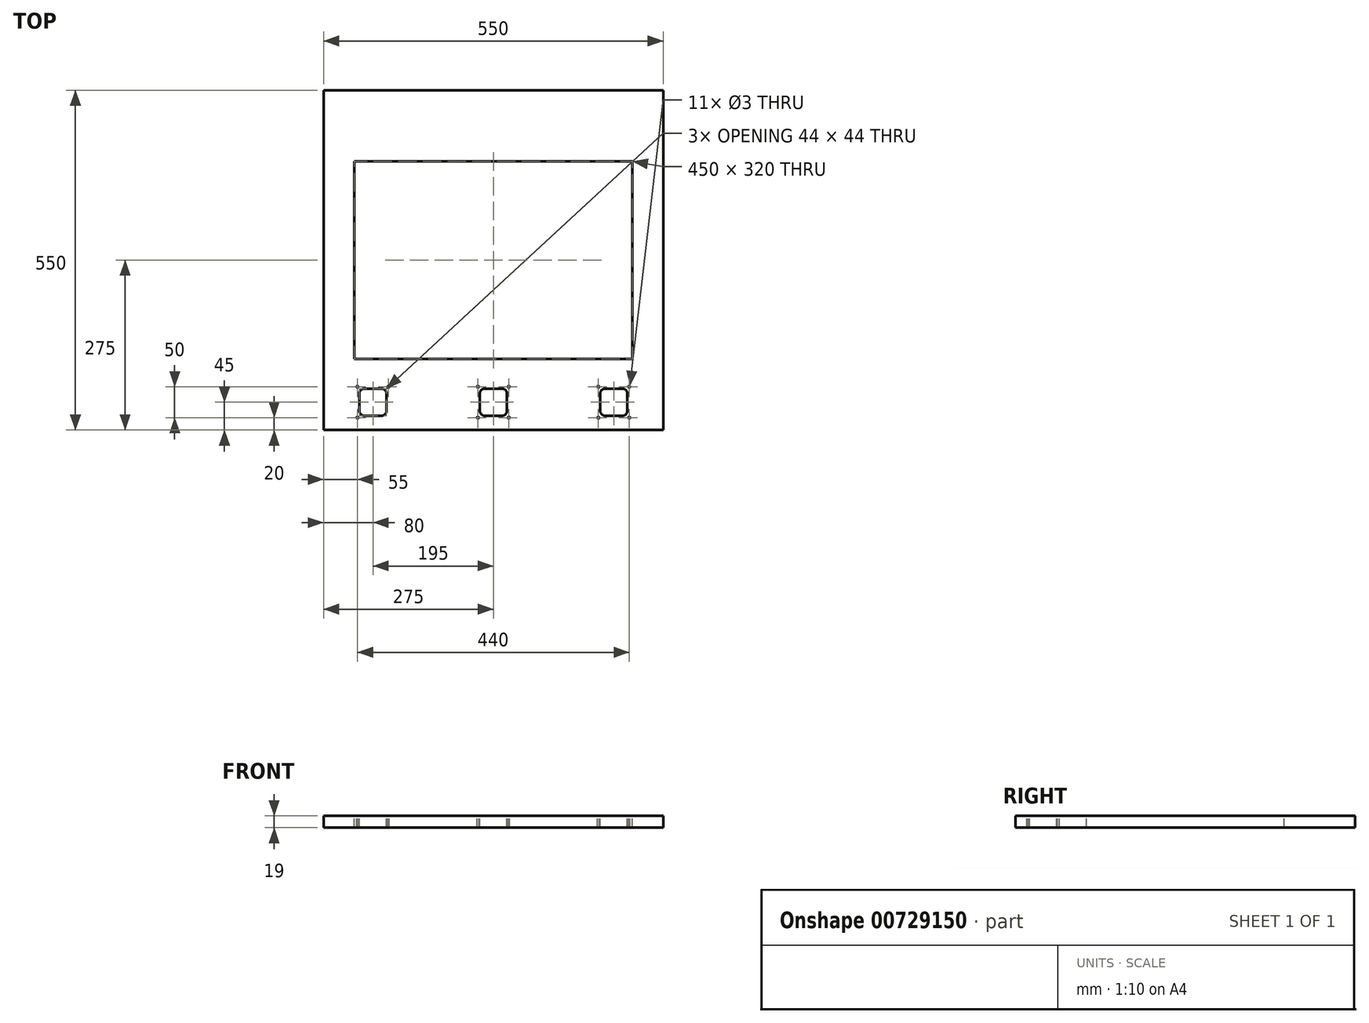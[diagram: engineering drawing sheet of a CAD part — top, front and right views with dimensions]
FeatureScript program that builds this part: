
annotation { "Feature Type Name" : "Feature", "Feature Type Description" : "" }
export const myFeature = defineFeature(function(context is Context, id is Id, definition is map)
    precondition{}
    {
        {
            var Q0;
            Q0=qCreatedBy(makeId("Top.planeOp"),FACE);
            var sketch = newSketch(context, id + "F0", { "sketchPlane" : qUnion([Q0])});
            skLineSegment(sketch, "E0.bottom", {"start": v(275, -275) * mm, "end": v(-275, -275) * mm});
            skLineSegment(sketch, "E0.top", {"start": v(275, 275) * mm, "end": v(-275, 275) * mm});
            skLineSegment(sketch, "E0.left", {"start": v(275, -275) * mm, "end": v(275, 275) * mm});
            skLineSegment(sketch, "E0.right", {"start": v(-275, -275) * mm, "end": v(-275, 275) * mm});
            skPoint(sketch, "E0.middle", {"position": v(0, 0) * mm});
            skSolve(sketch);
        }
        {
            var Q0;
            Q0=makeQuery(id+"F0.imprint","IMPRINT",FACE,{"disambiguationData":[TD([[makeQuery(id+"F0.imprint","IMPRINT",EDGE,{"derivedFrom":sQuery(id+"F0.wireOp",EDGE,"E0.bottom")}),-1.0]])]});
            extrude(context, id + "F1", {"entities" : qUnion([Q0]), "depth" : 19 * mm, "offsetDistance" : 25 * mm});
        }
        {
            var Q0;
            Q0=makeQuery(id+"F1.opExtrude","CAP_FACE",FACE,{"disambiguationData":[OSD([sQuery(id+"F0.wireOp",EDGE,"E0.bottom"),sQuery(id+"F0.wireOp",EDGE,"E0.top"),sQuery(id+"F0.wireOp",EDGE,"E0.left"),sQuery(id+"F0.wireOp",EDGE,"E0.right")])],"isStart":false});
            var sketch = newSketch(context, id + "F2", { "sketchPlane" : qUnion([Q0])});
            skLineSegment(sketch, "E1.bottom", {"start": v(225, -160) * mm, "end": v(-225, -160) * mm});
            skLineSegment(sketch, "E1.top", {"start": v(225, 160) * mm, "end": v(-225, 160) * mm});
            skLineSegment(sketch, "E1.left", {"start": v(225, -160) * mm, "end": v(225, 160) * mm});
            skLineSegment(sketch, "E1.right", {"start": v(-225, -160) * mm, "end": v(-225, 160) * mm});
            skPoint(sketch, "E1.middle", {"position": v(0, 0) * mm});
            skSolve(sketch);
        }
        {
            var Q0;
            Q0=makeQuery(id+"F2.imprint","IMPRINT",FACE,{"disambiguationData":[TD([[makeQuery(id+"F2.imprint","IMPRINT",EDGE,{"derivedFrom":sQuery(id+"F2.wireOp",EDGE,"E1.bottom")}),-1.0]])]});
            extrude(context, id + "F3", {"entities" : qUnion([Q0]), "operationType" : NewBodyOperationType.REMOVE, "oppositeDirection" : true, "depth" : 25 * mm, "offsetDistance" : 25 * mm});
        }
        {
            var Q0;
            Q0=makeQuery(id+"F1.opExtrude","CAP_FACE",FACE,{"disambiguationData":[OSD([sQuery(id+"F0.wireOp",EDGE,"E0.bottom"),sQuery(id+"F0.wireOp",EDGE,"E0.top"),sQuery(id+"F0.wireOp",EDGE,"E0.left"),sQuery(id+"F0.wireOp",EDGE,"E0.right")])],"isStart":false});
            var sketch = newSketch(context, id + "F4", { "sketchPlane" : qUnion([Q0])});
            skLineSegment(sketch, "E2.bottom", {"start": v(220, -205) * mm, "end": v(170, -205) * mm});
            skLineSegment(sketch, "E2.top", {"start": v(220, -255) * mm, "end": v(170, -255) * mm});
            skLineSegment(sketch, "E2.left", {"start": v(220, -205) * mm, "end": v(220, -255) * mm});
            skLineSegment(sketch, "E2.right", {"start": v(170, -205) * mm, "end": v(170, -255) * mm});
            skPoint(sketch, "E2.middle", {"position": v(195, -230) * mm});
            skLineSegment(sketch, "E3.bottom", {"start": v(217, -252) * mm, "end": v(173, -252) * mm});
            skLineSegment(sketch, "E3.top", {"start": v(217, -208) * mm, "end": v(173, -208) * mm});
            skLineSegment(sketch, "E3.left", {"start": v(217, -252) * mm, "end": v(217, -208) * mm});
            skLineSegment(sketch, "E3.right", {"start": v(173, -252) * mm, "end": v(173, -208) * mm});
            skLineSegment(sketch, "E4", {"start": v(0, 0) * mm, "end": v(0, -382.53) * mm});
            skLineSegment(sketch, "E5.MirrorCS", {"start": v(-220, -255) * mm, "end": v(-170, -255) * mm});
            skLineSegment(sketch, "E6.MirrorCS", {"start": v(-217, -252) * mm, "end": v(-173, -252) * mm});
            skLineSegment(sketch, "E7.MirrorCS", {"start": v(-217, -252) * mm, "end": v(-217, -208) * mm});
            skLineSegment(sketch, "E8.MirrorCS", {"start": v(-220, -205) * mm, "end": v(-220, -255) * mm});
            skLineSegment(sketch, "E9.MirrorCS", {"start": v(-170, -205) * mm, "end": v(-170, -255) * mm});
            skLineSegment(sketch, "E10.MirrorCS", {"start": v(-173, -252) * mm, "end": v(-173, -208) * mm});
            skLineSegment(sketch, "E11.MirrorCS", {"start": v(-217, -208) * mm, "end": v(-173, -208) * mm});
            skLineSegment(sketch, "E12.MirrorCS", {"start": v(-220, -205) * mm, "end": v(-170, -205) * mm});
            skPoint(sketch, "E13.MirrorP", {"position": v(-195, -230) * mm});
            skLineSegment(sketch, "E14.bottom", {"start": v(22, -252) * mm, "end": v(-22, -252) * mm});
            skLineSegment(sketch, "E14.top", {"start": v(22, -208) * mm, "end": v(-22, -208) * mm});
            skLineSegment(sketch, "E14.left", {"start": v(22, -252) * mm, "end": v(22, -208) * mm});
            skLineSegment(sketch, "E14.right", {"start": v(-22, -252) * mm, "end": v(-22, -208) * mm});
            skPoint(sketch, "E14.middle", {"position": v(0, -230) * mm});
            skLineSegment(sketch, "E15.bottom", {"start": v(25, -255) * mm, "end": v(-25, -255) * mm});
            skLineSegment(sketch, "E15.top", {"start": v(25, -205) * mm, "end": v(-25, -205) * mm});
            skLineSegment(sketch, "E15.left", {"start": v(25, -255) * mm, "end": v(25, -205) * mm});
            skLineSegment(sketch, "E15.right", {"start": v(-25, -255) * mm, "end": v(-25, -205) * mm});
            skLineSegment(sketch, "E16", {"start": v(0, -230) * mm, "end": v(195, -230) * mm, "construction": true});
            skSolve(sketch);
        }
        {
            var Q0;
            Q0=sQuery(id+"F4.wireOp",VERTEX,"E2.left.end");
            var Q1;
            Q1=sQuery(id+"F4.wireOp",VERTEX,"E2.bottom.start");
            var Q2;
            Q2=sQuery(id+"F4.wireOp",VERTEX,"E2.right.start");
            var Q3;
            Q3=sQuery(id+"F4.wireOp",VERTEX,"E2.right.end");
            var Q4;
            Q4=sQuery(id+"F4.wireOp",VERTEX,"E8.MirrorCS.start");
            var Q5;
            Q5=sQuery(id+"F4.wireOp",VERTEX,"E8.MirrorCS.end");
            var Q6;
            Q6=sQuery(id+"F4.wireOp",VERTEX,"E5.MirrorCS.end");
            var Q7;
            Q7=sQuery(id+"F4.wireOp",VERTEX,"E15.top.end");
            var Q8;
            Q8=sQuery(id+"F4.wireOp",VERTEX,"E15.right.start");
            var Q9;
            Q9=sQuery(id+"F4.wireOp",VERTEX,"E15.bottom.start");
            var Q10;
            Q10=sQuery(id+"F4.wireOp",VERTEX,"E15.left.end");
            var Q11;
            Q11=sQuery(id+"F4.wireOp",VERTEX,"E12.MirrorCS.end");
            var Q12;
            Q12=makeQuery(id+"F1.opExtrude","SWEPT_BODY",BODY,{"disambiguationData":[OSD([sQuery(id+"F0.wireOp",EDGE,"E0.bottom"),sQuery(id+"F0.wireOp",EDGE,"E0.top"),sQuery(id+"F0.wireOp",EDGE,"E0.left"),sQuery(id+"F0.wireOp",EDGE,"E0.right")])]});
            hole(context, id + "F5", {"style" : HoleStyle.SIMPLE, "endStyle" : HoleEndStyle.THROUGH, "holeDiameter" : 3 * mm, "majorDiameter" : 5 * mm, "isTappedThrough" : true, "tappedDepth" : 12 * mm, "tapClearance" : 3, "locations" : qUnion([Q0, Q1, Q2, Q3, Q4, Q5, Q6, Q7, Q8, Q9, Q10, Q11]), "scope" : qUnion([Q12])});
        }
        {
            var Q0;
            Q0=makeQuery(id+"F4.imprint","IMPRINT",FACE,{"disambiguationData":[TD([[makeQuery(id+"F4.imprint","IMPRINT",EDGE,{"derivedFrom":sQuery(id+"F4.wireOp",EDGE,"E3.bottom")}),-1.0]])]});
            var Q1;
            Q1=makeQuery(id+"F4.imprint","IMPRINT",FACE,{"disambiguationData":[TD([[makeQuery(id+"F4.imprint","IMPRINT",EDGE,{"derivedFrom":sQuery(id+"F4.wireOp",EDGE,"E7.MirrorCS")}),-1.0]])]});
            var Q2;
            {var subQ5=sQuery(id+"F4.wireOp",EDGE,"E14.left");Q2=makeQuery(id+"F4.imprint","IMPRINT",FACE,{"disambiguationData":[TD([[makeQuery(id+"F4.imprint","IMPRINT",EDGE,{"derivedFrom":subQ5}),1.0]])]});}
            var Q3;
            {var subQ5=sQuery(id+"F4.wireOp",EDGE,"E14.right");Q3=makeQuery(id+"F4.imprint","IMPRINT",FACE,{"disambiguationData":[TD([[makeQuery(id+"F4.imprint","IMPRINT",EDGE,{"derivedFrom":subQ5}),-1.0]])]});}
            extrude(context, id + "F6", {"entities" : qUnion([Q0, Q1, Q2, Q3]), "operationType" : NewBodyOperationType.REMOVE, "oppositeDirection" : true, "depth" : 25 * mm, "offsetDistance" : 25 * mm});
        }
        {
            var Q0;
            Q0=makeQuery(id+"F6.boolean.opBoolean","COPY",EDGE,{"derivedFrom":makeQuery(id+"F6.opExtrude","SWEPT_EDGE",EDGE,{"disambiguationData":[OSD([sQuery(id+"F4.wireOp",EDGE,"E3.top"),sQuery(id+"F4.wireOp",EDGE,"E3.right")])]})});
            var Q1;
            Q1=makeQuery(id+"F6.boolean.opBoolean","COPY",EDGE,{"derivedFrom":makeQuery(id+"F6.opExtrude","SWEPT_EDGE",EDGE,{"disambiguationData":[OSD([sQuery(id+"F4.wireOp",EDGE,"E3.top"),sQuery(id+"F4.wireOp",EDGE,"E3.left")])]})});
            var Q2;
            Q2=makeQuery(id+"F6.boolean.opBoolean","COPY",EDGE,{"derivedFrom":makeQuery(id+"F6.opExtrude","SWEPT_EDGE",EDGE,{"disambiguationData":[OSD([sQuery(id+"F4.wireOp",EDGE,"E3.bottom"),sQuery(id+"F4.wireOp",EDGE,"E3.right")])]})});
            var Q3;
            Q3=makeQuery(id+"F6.boolean.opBoolean","COPY",EDGE,{"derivedFrom":makeQuery(id+"F6.opExtrude","SWEPT_EDGE",EDGE,{"disambiguationData":[OSD([sQuery(id+"F4.wireOp",EDGE,"E3.bottom"),sQuery(id+"F4.wireOp",EDGE,"E3.left")])]})});
            var Q4;
            Q4=makeQuery(id+"F6.boolean.opBoolean","COPY",EDGE,{"derivedFrom":makeQuery(id+"F6.opExtrude","SWEPT_EDGE",EDGE,{"disambiguationData":[OSD([sQuery(id+"F4.wireOp",EDGE,"E7.MirrorCS"),sQuery(id+"F4.wireOp",EDGE,"E6.MirrorCS")])]})});
            var Q5;
            Q5=makeQuery(id+"F6.boolean.opBoolean","COPY",EDGE,{"derivedFrom":makeQuery(id+"F6.opExtrude","SWEPT_EDGE",EDGE,{"disambiguationData":[OSD([sQuery(id+"F4.wireOp",EDGE,"E7.MirrorCS"),sQuery(id+"F4.wireOp",EDGE,"E11.MirrorCS")])]})});
            var Q6;
            Q6=makeQuery(id+"F6.boolean.opBoolean","COPY",EDGE,{"derivedFrom":makeQuery(id+"F6.opExtrude","SWEPT_EDGE",EDGE,{"disambiguationData":[OSD([sQuery(id+"F4.wireOp",EDGE,"E10.MirrorCS"),sQuery(id+"F4.wireOp",EDGE,"E11.MirrorCS")])]})});
            var Q7;
            Q7=makeQuery(id+"F6.boolean.opBoolean","COPY",EDGE,{"derivedFrom":makeQuery(id+"F6.opExtrude","SWEPT_EDGE",EDGE,{"disambiguationData":[OSD([sQuery(id+"F4.wireOp",EDGE,"E6.MirrorCS"),sQuery(id+"F4.wireOp",EDGE,"E10.MirrorCS")])]})});
            var Q8;
            Q8=makeQuery(id+"F6.boolean.opBoolean","COPY",EDGE,{"derivedFrom":makeQuery(id+"F6.opExtrude","SWEPT_EDGE",EDGE,{"disambiguationData":[OSD([sQuery(id+"F4.wireOp",EDGE,"E14.bottom"),sQuery(id+"F4.wireOp",EDGE,"E14.right")])]})});
            var Q9;
            Q9=makeQuery(id+"F6.boolean.opBoolean","COPY",EDGE,{"derivedFrom":makeQuery(id+"F6.opExtrude","SWEPT_EDGE",EDGE,{"disambiguationData":[OSD([sQuery(id+"F4.wireOp",EDGE,"E14.bottom"),sQuery(id+"F4.wireOp",EDGE,"E14.left")])]})});
            var Q10;
            Q10=makeQuery(id+"F6.boolean.opBoolean","COPY",EDGE,{"derivedFrom":makeQuery(id+"F6.opExtrude","SWEPT_EDGE",EDGE,{"disambiguationData":[OSD([sQuery(id+"F4.wireOp",EDGE,"E14.top"),sQuery(id+"F4.wireOp",EDGE,"E14.left")])]})});
            var Q11;
            Q11=makeQuery(id+"F6.boolean.opBoolean","COPY",EDGE,{"derivedFrom":makeQuery(id+"F6.opExtrude","SWEPT_EDGE",EDGE,{"disambiguationData":[OSD([sQuery(id+"F4.wireOp",EDGE,"E14.top"),sQuery(id+"F4.wireOp",EDGE,"E14.right")])]})});
            fillet(context, id + "F7", {"entities" : qUnion([Q0, Q1, Q2, Q3, Q4, Q5, Q6, Q7, Q8, Q9, Q10, Q11]), "radius" : 8 * mm, "tangentPropagation" : true, "allowEdgeOverflow" : false});
        }
    });
